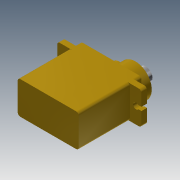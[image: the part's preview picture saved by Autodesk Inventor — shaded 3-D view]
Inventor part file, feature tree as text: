
AUTODESK INVENTOR PART (.ipt)
format: ipt  version: 2013 (Build 170138000, 138)  size: 224,256 bytes
history: native  units: mm
features: sketch x18, fillet x12, extrude x11
ambient origin geometry x8: Origin, YZ Plane, XZ Plane, XY Plane, X Axis, Y Axis, Z Axis, Center Point
bodies: Solid1 (feature_tree)
feature tree (41):
  extrude  "Extrusion1"  Depth=4.4mm TaperAngle=0.0deg
  sketch  "Sketch2"  dims[d11=4.4mm d12=0.0mm d18=7.9mm d19=0.0mm]
  sketch  "Sketch6"  dims[d20=7.9mm d21=0.0mm d22=7.9mm d23=0.0mm]
  extrude  "Extrusion2"  Depth=7.9mm TaperAngle=0.0deg
  sketch  "Sketch7"  dims[d26=4.0mm d27=0.0mm d28=5.0mm]
  sketch  "Sketch8"  dims[d29=3.0mm d30=0.0mm d31=3.0mm d32=0.0mm]
  sketch  "Sketch9"  dims[d39=3.0mm d40=0.0mm d43=3.0mm d44=0.0mm]
  extrude  "Extrusion3"  Depth=7.9mm TaperAngle=0.0deg
  sketch  "Sketch10"  dims[d45=1.0mm d46=1.0mm]
  sketch  "Sketch11"  dims[d47=1.0mm d48=1.0mm]
  extrude  "Extrusion4"  Depth=5.0mm
  extrude  "Extrusion5"  Depth=3.0mm TaperAngle=0.0deg
  extrude  "Extrusion6"  Depth=3.0mm TaperAngle=0.0deg
  extrude  "Extrusion7"  Depth=1.0mm
  extrude  "Extrusion8"  Depth=1.0mm
  extrude  "Extrusion9"  Depth=1.0mm
  sketch  "Sketch16"
  sketch  "Sketch17"
  sketch  "Sketch18"
  sketch  "Sketch19"
  extrude  "Extrusion10"  Depth=1.0mm
  extrude  "Extrusion11"  Depth=1.0mm
  fillet  "Fillet1"  Radius=1.0mm
  sketch  "Sketch20"
  fillet  "Fillet2"  Radius=1.0mm
  fillet  "Fillet3"  [1 undecoded]
  fillet  "Fillet4"  [1 undecoded]
  fillet  "Fillet5"  [1 undecoded]
  fillet  "Fillet6"  [1 undecoded]
  fillet  "Fillet7"  [1 undecoded]
  fillet  "Fillet8"  [1 undecoded]
  fillet  "Fillet9"  [1 undecoded]
  fillet  "Fillet10"  [1 undecoded]
  fillet  "Fillet11"  [1 undecoded]
  fillet  "Fillet12"  [1 undecoded]
  sketch  "Sketch21"
  sketch  "Sketch1"  dims[d2=31.7mm d3=0.0mm d7=4.4mm d8=0.0mm]
  sketch  "Sketch12"  dims[d49=1.0mm d50=1.0mm]
  sketch  "Sketch13"  dims[d51=1.0mm d52=1.0mm]
  sketch  "Sketch14"  dims[d53=1.0mm d54=1.0mm d55=1.0mm d56=1.0mm]
  sketch  "Sketch15"
note: 10 required parameter values undecoded (feature->parameter linkage not recoverable at this tier; creation-order binding heuristic only, values carry confidence <= 0.55)
